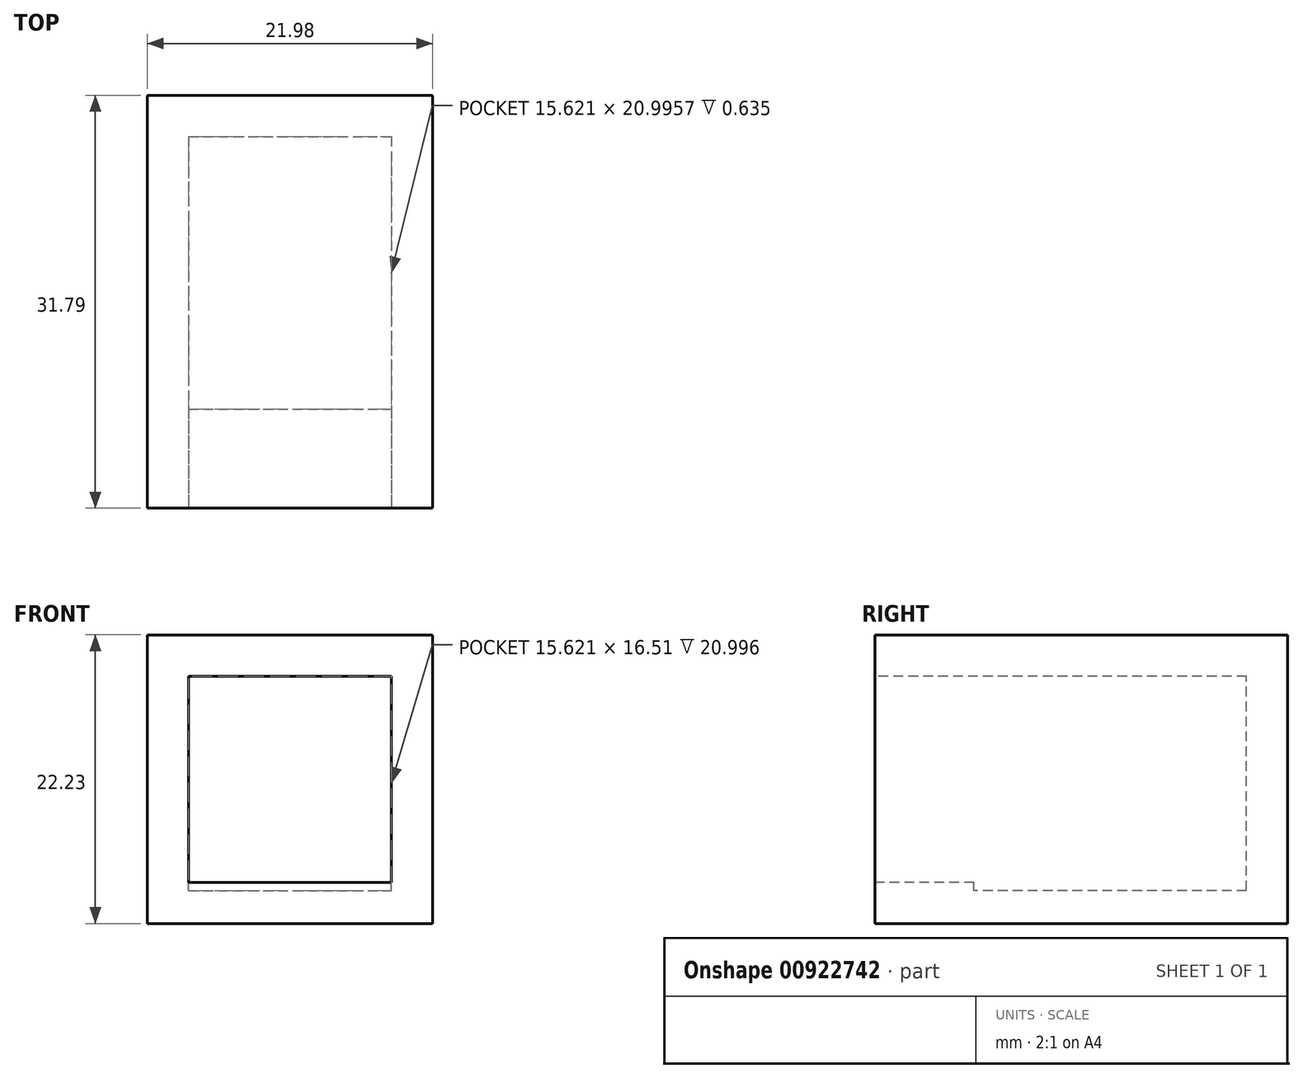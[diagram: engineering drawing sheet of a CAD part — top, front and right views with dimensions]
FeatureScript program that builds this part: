
annotation { "Feature Type Name" : "Feature", "Feature Type Description" : "" }
export const myFeature = defineFeature(function(context is Context, id is Id, definition is map)
    precondition{}
    {
        {
            assignVariable(context, id + "F0", {"name" : "padding", "anyValue" : 3.17 * mm});
        }
        {
            var Q0;
            Q0=qCreatedBy(makeId("Front.planeOp"),FACE);
            var sketch = newSketch(context, id + "F1", { "sketchPlane" : qUnion([Q0])});
            skLineSegment(sketch, "E0.bottom", {"start": v(-10.99, 0) * mm, "end": v(10.99, 0) * mm});
            skLineSegment(sketch, "E0.top", {"start": v(-10.99, 22.23) * mm, "end": v(10.99, 22.23) * mm});
            skLineSegment(sketch, "E0.left", {"start": v(-10.99, 0) * mm, "end": v(-10.99, 22.23) * mm});
            skLineSegment(sketch, "E0.right", {"start": v(10.99, 0) * mm, "end": v(10.99, 22.23) * mm});
            skLineSegment(sketch, "E1.bottom", {"start": v(-7.81, 2.54) * mm, "end": v(7.81, 2.54) * mm});
            skLineSegment(sketch, "E1.top", {"start": v(-7.81, 19.05) * mm, "end": v(7.81, 19.05) * mm});
            skLineSegment(sketch, "E1.left", {"start": v(-7.81, 2.54) * mm, "end": v(-7.81, 19.05) * mm});
            skLineSegment(sketch, "E1.right", {"start": v(7.81, 2.54) * mm, "end": v(7.81, 19.05) * mm});
            skLineSegment(sketch, "E2", {"start": v(-7.81, 3.18) * mm, "end": v(7.81, 3.17) * mm});
            skPoint(sketch, "E3", {"position": v(0, 2.54) * mm});
            skSolve(sketch);
        }
        {
            var Q0;
            Q0=qCreatedBy(makeId("Top.planeOp"),FACE);
            var sketch = newSketch(context, id + "F2", { "sketchPlane" : qUnion([Q0])});
            skLineSegment(sketch, "E4.bottom", {"start": v(-11, 0) * mm, "end": v(10.99, 0) * mm});
            skLineSegment(sketch, "E4.top", {"start": v(-11, 31.8) * mm, "end": v(10.99, 31.8) * mm});
            skLineSegment(sketch, "E4.left", {"start": v(-11, 0) * mm, "end": v(-11, 31.8) * mm});
            skLineSegment(sketch, "E4.right", {"start": v(10.99, 0) * mm, "end": v(10.99, 31.8) * mm});
            skSolve(sketch);
        }
        {
            var Q0;
            Q0 = qSketchRegion(id + "F2", true);
            extrude(context, id + "F3", {"entities" : qUnion([Q0]), "depth" : 22.22 * mm, "offsetDistance" : 25.4 * mm});
        }
        {
            var Q0;
            {var subQ0=sQuery(id+"F1.wireOp",EDGE,"E1.top");Q0=makeQuery(id+"F1.imprint","IMPRINT",FACE,{"disambiguationData":[TD([[makeQuery(id+"F1.imprint","IMPRINT",EDGE,{"derivedFrom":subQ0}),-1.0]])]});}
            var Q1;
            {var subQ0=sQuery(id+"F1.wireOp",EDGE,"E1.bottom");Q1=makeQuery(id+"F1.imprint","IMPRINT",FACE,{"disambiguationData":[TD([[makeQuery(id+"F1.imprint","IMPRINT",EDGE,{"derivedFrom":subQ0}),1.0]])]});}
            extrude(context, id + "F4", {"entities" : qUnion([Q0, Q1]), "operationType" : NewBodyOperationType.REMOVE, "endBound" : BoundingType.UP_TO_NEXT, "oppositeDirection" : true, "depth" : 50.8 * mm, "hasOffset" : true, "offsetDistance" : getVariable(context, 'padding')});
        }
        {
            var Q0;
            {var subQ0=sQuery(id+"F1.wireOp",EDGE,"E1.bottom");Q0=makeQuery(id+"F1.imprint","IMPRINT",FACE,{"disambiguationData":[TD([[makeQuery(id+"F1.imprint","IMPRINT",EDGE,{"derivedFrom":subQ0}),1.0]])]});}
            extrude(context, id + "F5", {"entities" : qUnion([Q0]), "operationType" : NewBodyOperationType.ADD, "oppositeDirection" : true, "depth" : 7.62 * mm, "offsetDistance" : 25.4 * mm});
        }
    });
